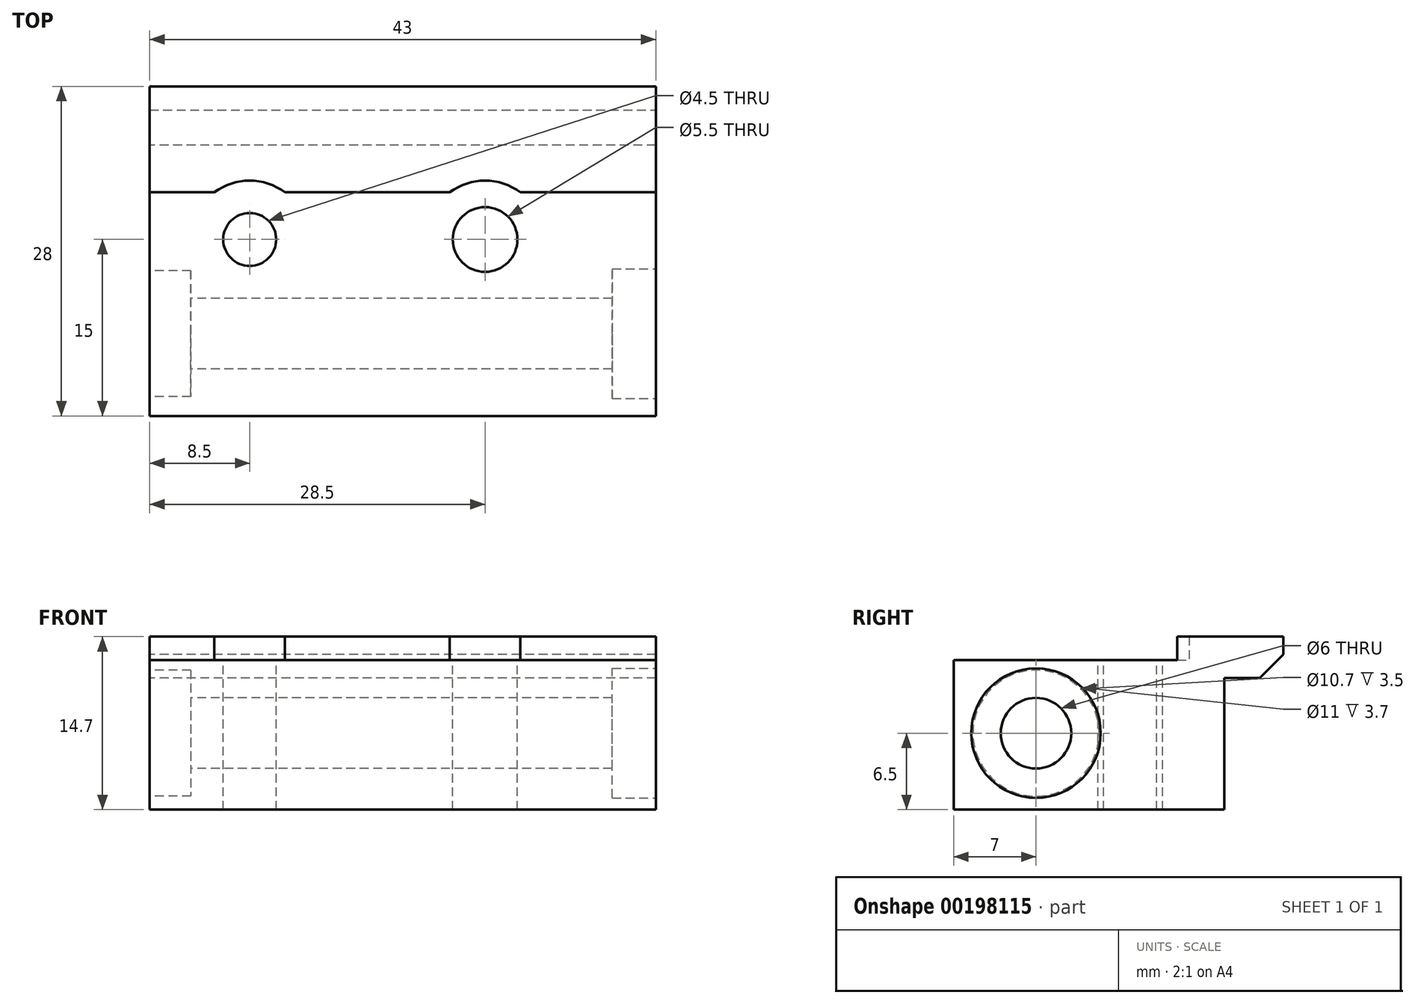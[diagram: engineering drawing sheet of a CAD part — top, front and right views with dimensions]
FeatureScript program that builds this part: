
annotation { "Feature Type Name" : "Feature", "Feature Type Description" : "" }
export const myFeature = defineFeature(function(context is Context, id is Id, definition is map)
    precondition{}
    {
        {
            var Q0;
            Q0=qCreatedBy(makeId("Top.planeOp"),FACE);
            var sketch = newSketch(context, id + "F0", { "sketchPlane" : qUnion([Q0])});
            skLineSegment(sketch, "E0.bottom", {"start": v(-21.5, 11.5) * mm, "end": v(21.5, 11.5) * mm});
            skLineSegment(sketch, "E0.top", {"start": v(-21.5, -11.5) * mm, "end": v(21.5, -11.5) * mm});
            skLineSegment(sketch, "E0.left", {"start": v(-21.5, 11.5) * mm, "end": v(-21.5, -11.5) * mm});
            skLineSegment(sketch, "E0.right", {"start": v(21.5, 11.5) * mm, "end": v(21.5, -11.5) * mm});
            skPoint(sketch, "E0.middle", {"position": v(0, 0) * mm});
            skSolve(sketch);
        }
        {
            var Q0;
            Q0 = qSketchRegion(id + "F0", true);
            extrude(context, id + "F1", {"entities" : qUnion([Q0]), "depth" : 12.7 * mm});
        }
        {
            var Q0;
            Q0=makeQuery(id+"F1.opExtrude","CAP_FACE",FACE,{"disambiguationData":[OSD([sQuery(id+"F0.wireOp",EDGE,"E0.bottom"),sQuery(id+"F0.wireOp",EDGE,"E0.top"),sQuery(id+"F0.wireOp",EDGE,"E0.left"),sQuery(id+"F0.wireOp",EDGE,"E0.right")])],"isStart":false});
            var sketch = newSketch(context, id + "F2", { "sketchPlane" : qUnion([Q0])});
            skCircle(sketch, "E1", {"center": v(7, 3.5) * mm, "radius": 2.75 * mm});
            skCircle(sketch, "E2", {"center": v(-13, 3.5) * mm, "radius": 2.25 * mm});
            skSolve(sketch);
        }
        {
            var Q0;
            Q0 = qSketchRegion(id + "F2", true);
            extrude(context, id + "F3", {"entities" : qUnion([Q0]), "operationType" : NewBodyOperationType.REMOVE, "oppositeDirection" : true, "depth" : 25.4 * mm});
        }
        {
            var Q0;
            Q0=makeQuery(id+"F1.opExtrude","SWEPT_FACE",FACE,{"disambiguationData":[OSD([sQuery(id+"F0.wireOp",EDGE,"E0.left")])]});
            var sketch = newSketch(context, id + "F4", { "sketchPlane" : qUnion([Q0])});
            skCircle(sketch, "E3", {"center": v(4.5, 6.5) * mm, "radius": 3 * mm});
            skSolve(sketch);
        }
        {
            var Q0;
            Q0 = qSketchRegion(id + "F4", true);
            extrude(context, id + "F5", {"entities" : qUnion([Q0]), "operationType" : NewBodyOperationType.REMOVE, "oppositeDirection" : true, "depth" : 50.8 * mm});
        }
        {
            var Q0;
            Q0=makeQuery(id+"F1.opExtrude","SWEPT_FACE",FACE,{"disambiguationData":[OSD([sQuery(id+"F0.wireOp",EDGE,"E0.left")])]});
            var sketch = newSketch(context, id + "F6", { "sketchPlane" : qUnion([Q0])});
            skCircle(sketch, "E4", {"center": v(4.5, 6.5) * mm, "radius": 5.35 * mm});
            skSolve(sketch);
        }
        {
            var Q0;
            Q0 = qSketchRegion(id + "F6", true);
            extrude(context, id + "F7", {"entities" : qUnion([Q0]), "operationType" : NewBodyOperationType.REMOVE, "oppositeDirection" : true, "depth" : 3.5 * mm});
        }
        {
            var Q0;
            Q0=makeQuery(id+"F1.opExtrude","SWEPT_FACE",FACE,{"disambiguationData":[OSD([sQuery(id+"F0.wireOp",EDGE,"E0.right")])]});
            var sketch = newSketch(context, id + "F8", { "sketchPlane" : qUnion([Q0])});
            skCircle(sketch, "E5", {"center": v(-4.5, 6.5) * mm, "radius": 5.5 * mm});
            skSolve(sketch);
        }
        {
            var Q0;
            Q0 = qSketchRegion(id + "F8", true);
            extrude(context, id + "F9", {"entities" : qUnion([Q0]), "operationType" : NewBodyOperationType.REMOVE, "oppositeDirection" : true, "depth" : 3.7 * mm});
        }
        {
            var Q0;
            Q0=makeQuery(id+"F1.opExtrude","CAP_FACE",FACE,{"disambiguationData":[OSD([sQuery(id+"F0.wireOp",EDGE,"E0.bottom"),sQuery(id+"F0.wireOp",EDGE,"E0.top"),sQuery(id+"F0.wireOp",EDGE,"E0.left"),sQuery(id+"F0.wireOp",EDGE,"E0.right")])],"isStart":false});
            var sketch = newSketch(context, id + "F10", { "sketchPlane" : qUnion([Q0])});
            skLineSegment(sketch, "E6.bottom", {"start": v(-21.5, 7.5) * mm, "end": v(21.5, 7.5) * mm});
            skLineSegment(sketch, "E6.top", {"start": v(-21.5, 11.5) * mm, "end": v(21.5, 11.5) * mm});
            skLineSegment(sketch, "E6.left", {"start": v(-21.5, 7.5) * mm, "end": v(-21.5, 11.5) * mm});
            skLineSegment(sketch, "E6.right", {"start": v(21.5, 7.5) * mm, "end": v(21.5, 11.5) * mm});
            skSolve(sketch);
        }
        {
            var Q0;
            Q0 = qSketchRegion(id + "F10", true);
            extrude(context, id + "F11", {"entities" : qUnion([Q0]), "operationType" : NewBodyOperationType.ADD, "depth" : 2 * mm});
        }
        {
            var Q0;
            Q0=makeQuery(id+"F11.boolean.opBoolean","MERGE",FACE,{"derivedFrom":[makeQuery(id+"F1.opExtrude","SWEPT_FACE",FACE,{"disambiguationData":[OSD([sQuery(id+"F0.wireOp",EDGE,"E0.bottom")])]}),makeQuery(id+"F11.opExtrude","SWEPT_FACE",FACE,{"disambiguationData":[OSD([sQuery(id+"F10.wireOp",EDGE,"E6.top")])]})]});
            var sketch = newSketch(context, id + "F12", { "sketchPlane" : qUnion([Q0])});
            skLineSegment(sketch, "E7.bottom", {"start": v(-21.5, 14.7) * mm, "end": v(21.5, 14.7) * mm});
            skLineSegment(sketch, "E7.top", {"start": v(-21.5, 11.2) * mm, "end": v(21.5, 11.2) * mm});
            skLineSegment(sketch, "E7.left", {"start": v(-21.5, 14.7) * mm, "end": v(-21.5, 11.2) * mm});
            skLineSegment(sketch, "E7.right", {"start": v(21.5, 14.7) * mm, "end": v(21.5, 11.2) * mm});
            skSolve(sketch);
        }
        {
            var Q0;
            Q0 = qSketchRegion(id + "F12", true);
            extrude(context, id + "F13", {"entities" : qUnion([Q0]), "operationType" : NewBodyOperationType.ADD, "depth" : 5 * mm});
        }
        {
            var Q0;
            Q0=makeQuery(id+"F13.opExtrude","CAP_EDGE",EDGE,{"disambiguationData":[OSD([sQuery(id+"F12.wireOp",EDGE,"E7.top")])],"isStart":false});
            chamfer(context, id + "F14", {"entities" : qUnion([Q0]), "width" : 2 * mm, "tangentPropagation" : true});
        }
        {
            var Q0;
            Q0=makeQuery(id+"F1.opExtrude","CAP_FACE",FACE,{"disambiguationData":[OSD([sQuery(id+"F0.wireOp",EDGE,"E0.bottom"),sQuery(id+"F0.wireOp",EDGE,"E0.top"),sQuery(id+"F0.wireOp",EDGE,"E0.left"),sQuery(id+"F0.wireOp",EDGE,"E0.right")])],"isStart":false});
            var sketch = newSketch(context, id + "F15", { "sketchPlane" : qUnion([Q0])});
            skCircle(sketch, "E8", {"center": v(-13, 3.5) * mm, "radius": 5 * mm});
            skCircle(sketch, "E9", {"center": v(7, 3.5) * mm, "radius": 5 * mm});
            skSolve(sketch);
        }
        {
            var Q0;
            Q0 = qSketchRegion(id + "F15", true);
            extrude(context, id + "F16", {"entities" : qUnion([Q0]), "operationType" : NewBodyOperationType.REMOVE, "depth" : 25 * mm});
        }
    });
